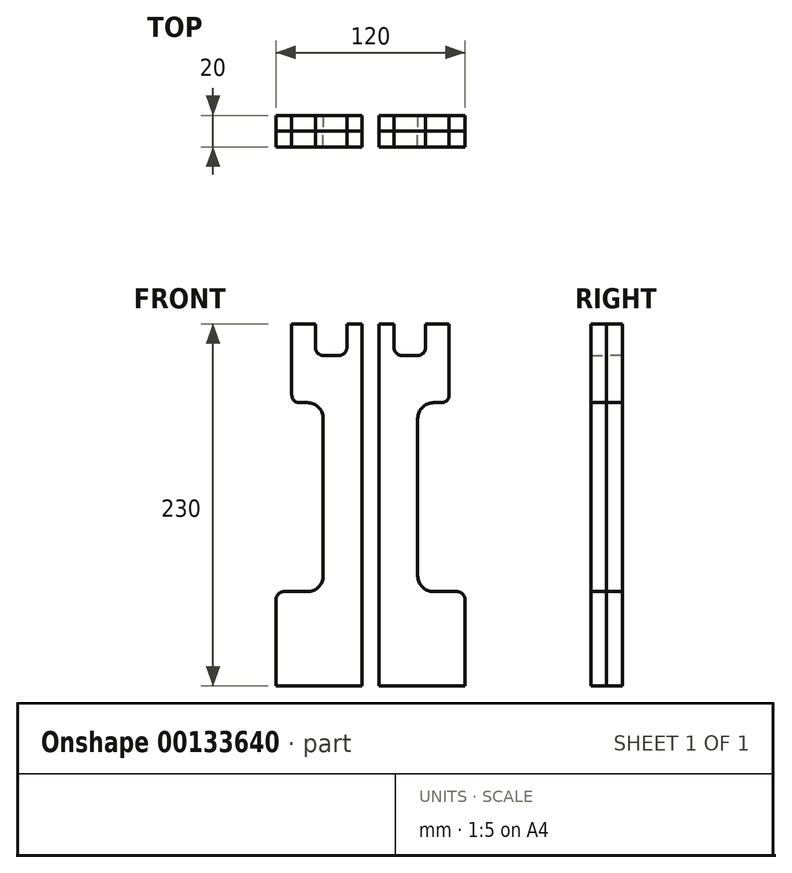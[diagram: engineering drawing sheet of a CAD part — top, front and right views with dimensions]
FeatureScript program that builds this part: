
annotation { "Feature Type Name" : "Feature", "Feature Type Description" : "" }
export const myFeature = defineFeature(function(context is Context, id is Id, definition is map)
    precondition{}
    {
        {
            var Q0;
            Q0=qCreatedBy(makeId("Front.planeOp"),FACE);
            var sketch = newSketch(context, id + "F0", { "sketchPlane" : qUnion([Q0])});
            skLineSegment(sketch, "E0.bottom", {"start": v(-40, 30) * mm, "end": v(-55, 30) * mm});
            skLineSegment(sketch, "E0.top", {"start": v(60, -30) * mm, "end": v(-60, -30) * mm});
            skLineSegment(sketch, "E0.left", {"start": v(60, 25) * mm, "end": v(60, -30) * mm});
            skLineSegment(sketch, "E0.right", {"start": v(-60, 25) * mm, "end": v(-60, -30) * mm});
            skPoint(sketch, "E0.middle", {"position": v(0, 0) * mm});
            skLineSegment(sketch, "E1.bottom", {"start": v(-30, 30) * mm, "end": v(30, 30) * mm});
            skLineSegment(sketch, "E1.top", {"start": v(-30, 150) * mm, "end": v(30, 150) * mm});
            skLineSegment(sketch, "E1.left", {"start": v(-30, 40) * mm, "end": v(-30, 140) * mm});
            skLineSegment(sketch, "E1.right", {"start": v(30, 40) * mm, "end": v(30, 140) * mm});
            skPoint(sketch, "E1.middle", {"position": v(0, 90) * mm});
            skLineSegment(sketch, "E2", {"start": v(40, 150) * mm, "end": v(45, 150) * mm});
            skLineSegment(sketch, "E3", {"start": v(50, 155) * mm, "end": v(50, 200) * mm});
            skLineSegment(sketch, "E4", {"start": v(50, 200) * mm, "end": v(35, 200) * mm});
            skLineSegment(sketch, "E5", {"start": v(35, 200) * mm, "end": v(35, 185) * mm});
            skLineSegment(sketch, "E6", {"start": v(30, 180) * mm, "end": v(20, 180) * mm});
            skLineSegment(sketch, "E7", {"start": v(15, 185) * mm, "end": v(15, 200) * mm});
            skLineSegment(sketch, "E8", {"start": v(15, 200) * mm, "end": v(-15, 200) * mm});
            skLineSegment(sketch, "E9", {"start": v(-15, 200) * mm, "end": v(-15, 185) * mm});
            skLineSegment(sketch, "E10", {"start": v(-20, 180) * mm, "end": v(-30, 180) * mm});
            skLineSegment(sketch, "E11", {"start": v(-35, 185) * mm, "end": v(-35, 200) * mm});
            skLineSegment(sketch, "E12", {"start": v(-35, 200) * mm, "end": v(-50, 200) * mm});
            skLineSegment(sketch, "E13", {"start": v(-50, 200) * mm, "end": v(-50, 155) * mm});
            skLineSegment(sketch, "E14", {"start": v(-45, 150) * mm, "end": v(-40, 150) * mm});
            skLineSegment(sketch, "E15.bottom", {"start": v(-5.5, -30) * mm, "end": v(5.5, -30) * mm});
            skLineSegment(sketch, "E15.top", {"start": v(-5.5, 85) * mm, "end": v(5.5, 85) * mm});
            skLineSegment(sketch, "E15.left", {"start": v(-5.5, -30) * mm, "end": v(-5.5, 85) * mm});
            skLineSegment(sketch, "E15.right", {"start": v(5.5, -30) * mm, "end": v(5.5, 85) * mm});
            skPoint(sketch, "E15.middle", {"position": v(0, 27.5) * mm});
            skLineSegment(sketch, "E16.bottom", {"start": v(5.5, 85) * mm, "end": v(-5.5, 85) * mm});
            skLineSegment(sketch, "E16.top", {"start": v(5.5, 200) * mm, "end": v(-5.5, 200) * mm});
            skLineSegment(sketch, "E16.left", {"start": v(5.5, 85) * mm, "end": v(5.5, 200) * mm});
            skLineSegment(sketch, "E16.right", {"start": v(-5.5, 85) * mm, "end": v(-5.5, 200) * mm});
            skPoint(sketch, "E16.middle", {"position": v(0, 142.5) * mm});
            skPoint(sketch, "E16.middle.positionSnap0", {"position": v(0, 150) * mm});
            skPoint(sketch, "E16.centerSnap0", {"position": v(0, 150) * mm});
            skPoint(sketch, "E17.visualSharp", {"position": v(-35, 180) * mm});
            skArc(sketch, "E17.filletArc", {"start": v(-35, 185) * mm, "mid": v(-33.54, 181.46) * mm, "end": v(-30, 180) * mm});
            skPoint(sketch, "E18.visualSharp", {"position": v(-15, 180) * mm});
            skArc(sketch, "E18.filletArc", {"start": v(-20, 180) * mm, "mid": v(-16.46, 181.46) * mm, "end": v(-15, 185) * mm});
            skPoint(sketch, "E19.visualSharp", {"position": v(15, 180) * mm});
            skArc(sketch, "E19.filletArc", {"start": v(15, 185) * mm, "mid": v(16.46, 181.46) * mm, "end": v(20, 180) * mm});
            skPoint(sketch, "E20.visualSharp", {"position": v(35, 180) * mm});
            skArc(sketch, "E20.filletArc", {"start": v(30, 180) * mm, "mid": v(33.54, 181.46) * mm, "end": v(35, 185) * mm});
            skPoint(sketch, "E21.visualSharp", {"position": v(50, 150) * mm});
            skArc(sketch, "E21.filletArc", {"start": v(45, 150) * mm, "mid": v(48.54, 151.46) * mm, "end": v(50, 155) * mm});
            skPoint(sketch, "E22.visualSharp", {"position": v(-50, 150) * mm});
            skArc(sketch, "E22.filletArc", {"start": v(-50, 155) * mm, "mid": v(-48.54, 151.46) * mm, "end": v(-45, 150) * mm});
            skPoint(sketch, "E23.visualSharp", {"position": v(-60, 30) * mm});
            skArc(sketch, "E23.filletArc", {"start": v(-55, 30) * mm, "mid": v(-58.54, 28.54) * mm, "end": v(-60, 25) * mm});
            skPoint(sketch, "E24.visualSharp", {"position": v(60, 30) * mm});
            skArc(sketch, "E24.filletArc", {"start": v(60, 25) * mm, "mid": v(58.54, 28.54) * mm, "end": v(55, 30) * mm});
            skPoint(sketch, "E25.visualSharp", {"position": v(30, 150) * mm});
            skArc(sketch, "E25.filletArc", {"start": v(40, 150) * mm, "mid": v(32.93, 147.07) * mm, "end": v(30, 140) * mm});
            skPoint(sketch, "E26.visualSharp", {"position": v(-30, 150) * mm});
            skArc(sketch, "E26.filletArc", {"start": v(-30, 140) * mm, "mid": v(-32.93, 147.07) * mm, "end": v(-40, 150) * mm});
            skArc(sketch, "E27.filletArc", {"start": v(-40, 30) * mm, "mid": v(-32.93, 32.93) * mm, "end": v(-30, 40) * mm});
            skLineSegment(sketch, "E28", {"start": v(40, 30) * mm, "end": v(55, 30) * mm});
            skPoint(sketch, "E29.visualSharp", {"position": v(30, 30) * mm});
            skArc(sketch, "E29.filletArc", {"start": v(30, 40) * mm, "mid": v(32.93, 32.93) * mm, "end": v(40, 30) * mm});
            skSolve(sketch);
        }
        {
            var Q0;
            {var subQ5=sQuery(id+"F0.wireOp",EDGE,"E16.bottom");Q0=makeQuery(id+"F0.imprint","IMPRINT",FACE,{"disambiguationData":[TD([[makeQuery(id+"F0.imprint","IMPRINT",EDGE,{"derivedFrom":subQ5}),-1.0]])]});}
            var Q1;
            Q1=makeQuery(id+"F0.imprint","IMPRINT",FACE,{"disambiguationData":[TD([[makeQuery(id+"F0.imprint","IMPRINT",EDGE,{"derivedFrom":sQuery(id+"F0.wireOp",EDGE,"E0.bottom")}),1.0]])]});
            var Q2;
            {var subQ5=sQuery(id+"F0.wireOp",EDGE,"E16.top");Q2=makeQuery(id+"F0.imprint","IMPRINT",FACE,{"disambiguationData":[TD([[makeQuery(id+"F0.imprint","IMPRINT",EDGE,{"derivedFrom":subQ5}),1.0]])]});}
            var Q3;
            {var subQ4=sQuery(id+"F0.wireOp",EDGE,"E0.left");Q3=makeQuery(id+"F0.imprint","IMPRINT",FACE,{"disambiguationData":[TD([[makeQuery(id+"F0.imprint","IMPRINT",EDGE,{"derivedFrom":subQ4}),-1.0]])]});}
            extrude(context, id + "F1", {"entities" : qUnion([Q0, Q1, Q2, Q3]), "depth" : 10 * mm});
        }
        {
            var Q0;
            {var subQ5=sQuery(id+"F0.wireOp",EDGE,"E15.bottom");Q0=makeQuery(id+"F0.imprint","IMPRINT",FACE,{"disambiguationData":[TD([[makeQuery(id+"F0.imprint","IMPRINT",EDGE,{"derivedFrom":subQ5}),1.0]])]});}
            var Q1;
            Q1=makeQuery(id+"F0.imprint","IMPRINT",FACE,{"disambiguationData":[TD([[makeQuery(id+"F0.imprint","IMPRINT",EDGE,{"derivedFrom":sQuery(id+"F0.wireOp",EDGE,"E0.bottom")}),1.0]])]});
            var Q2;
            {var subQ4=sQuery(id+"F0.wireOp",EDGE,"E0.left");Q2=makeQuery(id+"F0.imprint","IMPRINT",FACE,{"disambiguationData":[TD([[makeQuery(id+"F0.imprint","IMPRINT",EDGE,{"derivedFrom":subQ4}),-1.0]])]});}
            var Q3;
            {var subQ5=sQuery(id+"F0.wireOp",EDGE,"E16.bottom");Q3=makeQuery(id+"F0.imprint","IMPRINT",FACE,{"disambiguationData":[TD([[makeQuery(id+"F0.imprint","IMPRINT",EDGE,{"derivedFrom":subQ5}),1.0]])]});}
            extrude(context, id + "F2", {"entities" : qUnion([Q0, Q1, Q2, Q3]), "oppositeDirection" : true, "depth" : 10 * mm});
        }
    });
